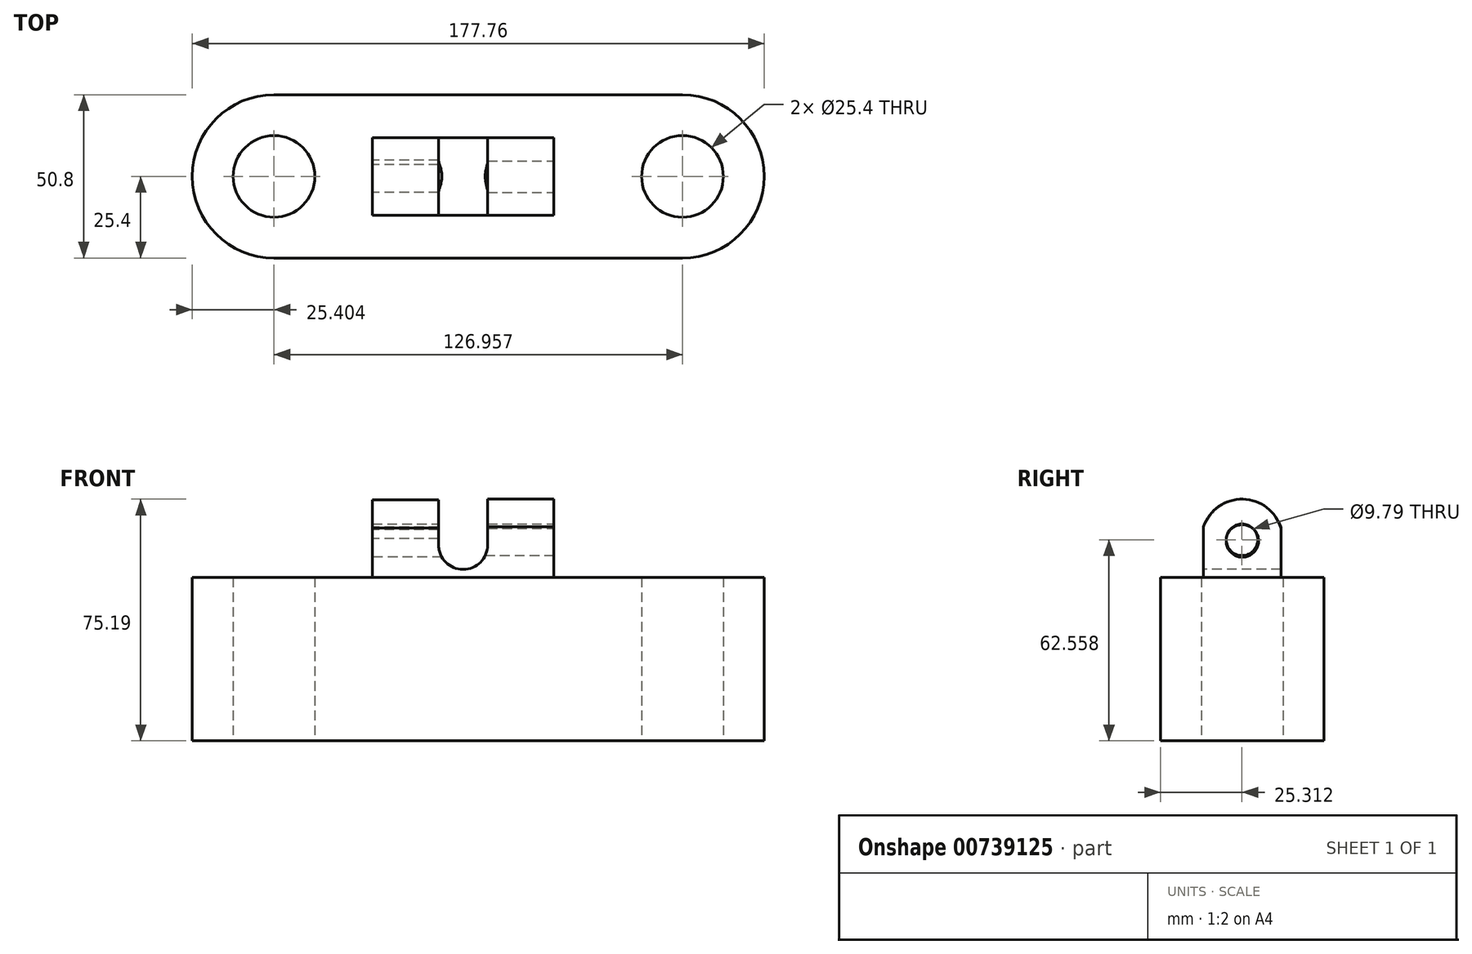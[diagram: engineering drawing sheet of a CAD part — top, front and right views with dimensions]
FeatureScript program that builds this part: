
annotation { "Feature Type Name" : "Feature", "Feature Type Description" : "" }
export const myFeature = defineFeature(function(context is Context, id is Id, definition is map)
    precondition{}
    {
        {
            var Q0;
            Q0=qCreatedBy(makeId("Top.planeOp"),FACE);
            var sketch = newSketch(context, id + "F0", { "sketchPlane" : qUnion([Q0])});
            skArc(sketch, "E0", {"start": v(-58.78, 25.4) * mm, "mid": v(-84.18, 0) * mm, "end": v(-58.78, -25.4) * mm});
            skArc(sketch, "E1", {"start": v(68.18, -25.4) * mm, "mid": v(93.58, 0) * mm, "end": v(68.18, 25.4) * mm});
            skLineSegment(sketch, "E2", {"start": v(-58.78, 25.4) * mm, "end": v(68.18, 25.4) * mm});
            skLineSegment(sketch, "E3", {"start": v(68.18, -25.4) * mm, "end": v(-58.78, -25.4) * mm});
            skCircle(sketch, "E4", {"center": v(-58.78, 0) * mm, "radius": 12.7 * mm});
            skCircle(sketch, "E5", {"center": v(68.18, 0) * mm, "radius": 12.7 * mm});
            skSolve(sketch);
        }
        {
            var Q0;
            Q0=makeQuery(id+"F0.imprint","IMPRINT",FACE,{"disambiguationData":[TD([[makeQuery(id+"F0.imprint","IMPRINT",EDGE,{"derivedFrom":sQuery(id+"F0.wireOp",EDGE,"E0")}),1.0]])]});
            extrude(context, id + "F1", {"entities" : qUnion([Q0]), "depth" : 50.8 * mm, "offsetDistance" : 25.4 * mm});
        }
        {
            var Q0;
            Q0=makeQuery(id+"F1.opExtrude","CAP_FACE",FACE,{"disambiguationData":[OSD([sQuery(id+"F0.wireOp",EDGE,"E0"),sQuery(id+"F0.wireOp",EDGE,"E1"),sQuery(id+"F0.wireOp",EDGE,"E2"),sQuery(id+"F0.wireOp",EDGE,"E3"),sQuery(id+"F0.wireOp",EDGE,"E4"),sQuery(id+"F0.wireOp",EDGE,"E5")])],"isStart":false});
            var sketch = newSketch(context, id + "F2", { "sketchPlane" : qUnion([Q0])});
            skLineSegment(sketch, "E6.bottom", {"start": v(28.16, 12.04) * mm, "end": v(-28.16, 12.04) * mm});
            skLineSegment(sketch, "E6.top", {"start": v(28.16, -12.04) * mm, "end": v(-28.16, -12.04) * mm});
            skLineSegment(sketch, "E6.left", {"start": v(28.16, 12.04) * mm, "end": v(28.16, -12.04) * mm});
            skLineSegment(sketch, "E6.right", {"start": v(-28.16, 12.04) * mm, "end": v(-28.16, -12.04) * mm});
            skPoint(sketch, "E6.middle", {"position": v(0, 0) * mm});
            skSolve(sketch);
        }
        {
            var Q0;
            Q0=makeQuery(id+"F2.imprint","IMPRINT",FACE,{"disambiguationData":[TD([[makeQuery(id+"F2.imprint","IMPRINT",EDGE,{"derivedFrom":sQuery(id+"F2.wireOp",EDGE,"E6.bottom")}),1.0]])]});
            extrude(context, id + "F3", {"entities" : qUnion([Q0]), "operationType" : NewBodyOperationType.ADD, "depth" : 25.4 * mm, "offsetDistance" : 25.4 * mm});
        }
        {
            var Q0;
            Q0=makeQuery(id+"F3.opExtrude","SWEPT_FACE",FACE,{"disambiguationData":[OSD([sQuery(id+"F2.wireOp",EDGE,"E6.top")])]});
            var sketch = newSketch(context, id + "F4", { "sketchPlane" : qUnion([Q0])});
            skArc(sketch, "E7", {"start": v(-7.62, 60.96) * mm, "mid": v(0, 53.34) * mm, "end": v(7.62, 60.96) * mm});
            skLineSegment(sketch, "E8", {"start": v(-7.62, 76.2) * mm, "end": v(-7.62, 60.96) * mm});
            skLineSegment(sketch, "E9", {"start": v(7.62, 60.96) * mm, "end": v(7.62, 76.2) * mm});
            skSolve(sketch);
        }
        {
            var Q0;
            Q0=makeQuery(id+"F4.imprint","IMPRINT",FACE,{"disambiguationData":[TD([[makeQuery(id+"F4.imprint","IMPRINT",EDGE,{"derivedFrom":sQuery(id+"F4.wireOp",EDGE,"E7")}),1.0]])]});
            extrude(context, id + "F5", {"entities" : qUnion([Q0]), "operationType" : NewBodyOperationType.REMOVE, "oppositeDirection" : true, "depth" : 34.54 * mm, "offsetDistance" : 25.4 * mm});
        }
        {
            var Q0;
            Q0=makeQuery(id+"F3.opExtrude","SWEPT_FACE",FACE,{"disambiguationData":[OSD([sQuery(id+"F2.wireOp",EDGE,"E6.right")])]});
            var sketch = newSketch(context, id + "F6", { "sketchPlane" : qUnion([Q0])});
            skArc(sketch, "E10", {"start": v(12.04, 66.28) * mm, "mid": v(0.07, 74.94) * mm, "end": v(-12.04, 66.46) * mm});
            skCircle(sketch, "E11", {"center": v(-0.03, 62.2) * mm, "radius": 5.05 * mm});
            skSolve(sketch);
        }
        {
            var Q0;
            Q0=makeQuery(id+"F3.opExtrude","SWEPT_FACE",FACE,{"disambiguationData":[OSD([sQuery(id+"F2.wireOp",EDGE,"E6.left")])]});
            var sketch = newSketch(context, id + "F7", { "sketchPlane" : qUnion([Q0])});
            skArc(sketch, "E12", {"start": v(12.04, 66.1) * mm, "mid": v(0.2, 75.19) * mm, "end": v(-12.04, 66.64) * mm});
            skCircle(sketch, "E13", {"center": v(-0.09, 62.56) * mm, "radius": 4.9 * mm});
            skSolve(sketch);
        }
        {
            var Q0;
            {var subQ0=sQuery(id+"F7.wireOp",EDGE,"E12");Q0=makeQuery(id+"F7.imprint","IMPRINT",FACE,{"disambiguationData":[TD([[makeQuery(id+"F7.imprint","IMPRINT",EDGE,{"derivedFrom":subQ0}),-1.0]])]});}
            extrude(context, id + "F8", {"entities" : qUnion([Q0]), "operationType" : NewBodyOperationType.REMOVE, "oppositeDirection" : true, "depth" : 25.4 * mm, "offsetDistance" : 25.4 * mm});
        }
        {
            var Q0;
            Q0=makeQuery(id+"F7.imprint","IMPRINT",FACE,{"disambiguationData":[TD([[makeQuery(id+"F7.imprint","IMPRINT",EDGE,{"derivedFrom":sQuery(id+"F7.wireOp",EDGE,"E13")}),1.0]])]});
            extrude(context, id + "F9", {"entities" : qUnion([Q0]), "operationType" : NewBodyOperationType.REMOVE, "oppositeDirection" : true, "depth" : 127 * mm, "offsetDistance" : 25.4 * mm});
        }
        {
            var Q0;
            {var subQ0=sQuery(id+"F6.wireOp",EDGE,"E10");Q0=makeQuery(id+"F6.imprint","IMPRINT",FACE,{"disambiguationData":[TD([[makeQuery(id+"F6.imprint","IMPRINT",EDGE,{"derivedFrom":subQ0}),-1.0]])]});}
            var Q1;
            Q1=makeQuery(id+"F6.imprint","IMPRINT",FACE,{"disambiguationData":[TD([[makeQuery(id+"F6.imprint","IMPRINT",EDGE,{"derivedFrom":sQuery(id+"F6.wireOp",EDGE,"E11")}),1.0]])]});
            extrude(context, id + "F10", {"entities" : qUnion([Q0, Q1]), "operationType" : NewBodyOperationType.REMOVE, "oppositeDirection" : true, "depth" : 25.4 * mm, "offsetDistance" : 25.4 * mm});
        }
    });
